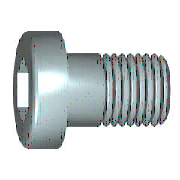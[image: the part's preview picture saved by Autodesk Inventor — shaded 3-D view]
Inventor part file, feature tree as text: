
AUTODESK INVENTOR PART (.ipt)
format: ipt  version: 2020 (Build 240168000, 168)  size: 189,952 bytes
history: native  units: mm (DEFAULTED — no unit token found)
features: sketch x2, other x2, chamfer x1, extrude x1, plane x1
ambient origin geometry x7: Origin, YZ Plane, XY Plane, X Axis, Y Axis, Z Axis, Center Point
bodies: Solid1 (feature_tree)
feature tree (7):
  sketch  "Skizze1"  dims[d0=2.8mm]
  other  "Körper"
  chamfer  "Fase2"  Angle=60.0deg  [1 undecoded]
  extrude  "Loch"  Depth=2.0mm
  other  "Work Axis1"
  plane  "Work Plane1"
  sketch  "Skizze2"  dims[d1=1.6mm d2=60.0deg d3=4.0mm d4=3.464102mm d5=7.0mm d10=90.0deg d11=10.0mm d6=0.0mm d7=12.5mm d8=0.0mm d9=0.429415mm d12=0.429415mm d14=0.0mm d15=3.3mm d16=2.0mm d17=16.0mm d28=45.0deg d30=0.0mm d31=0.0mm d32=45.0deg d33=0.4mm d34=90.0deg]
note: 1 required parameter value undecoded (feature->parameter linkage not recoverable at this tier; creation-order binding heuristic only, values carry confidence <= 0.55)
